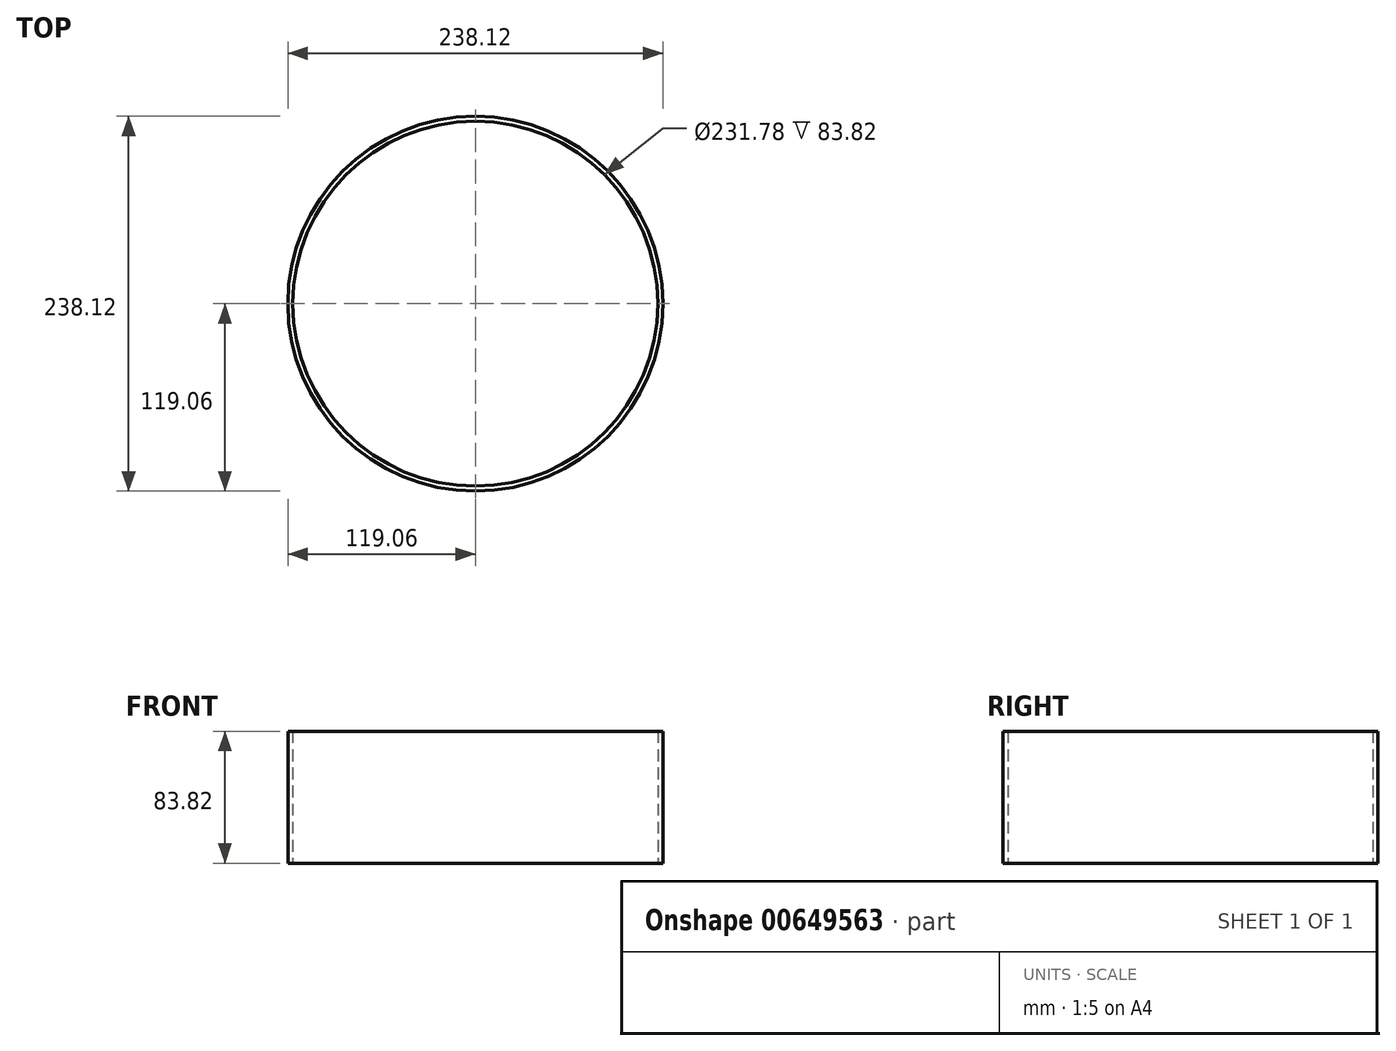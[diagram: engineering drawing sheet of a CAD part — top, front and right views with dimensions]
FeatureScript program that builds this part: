
annotation { "Feature Type Name" : "Feature", "Feature Type Description" : "" }
export const myFeature = defineFeature(function(context is Context, id is Id, definition is map)
    precondition{}
    {
        {
            var Q0;
            Q0=qCreatedBy(makeId("Top.planeOp"), FACE);
            var sketch = newSketch(context, id + "F0", { "sketchPlane" : qUnion([Q0])});
            skCircle(sketch, "E0", {"center": v(0, 0) * mm, "radius": 119.06 * mm});
            skCircle(sketch, "E1", {"center": v(0, 0) * mm, "radius": 115.89 * mm});
            skSolve(sketch);
        }
        {
            var Q0;
            Q0 = qSketchRegion(id + "F0", true);
            extrude(context, id + "F1", {"entities" : qUnion([Q0]), "depth" : 83.82 * mm, "offsetDistance" : 25.4 * mm});
        }
    });
